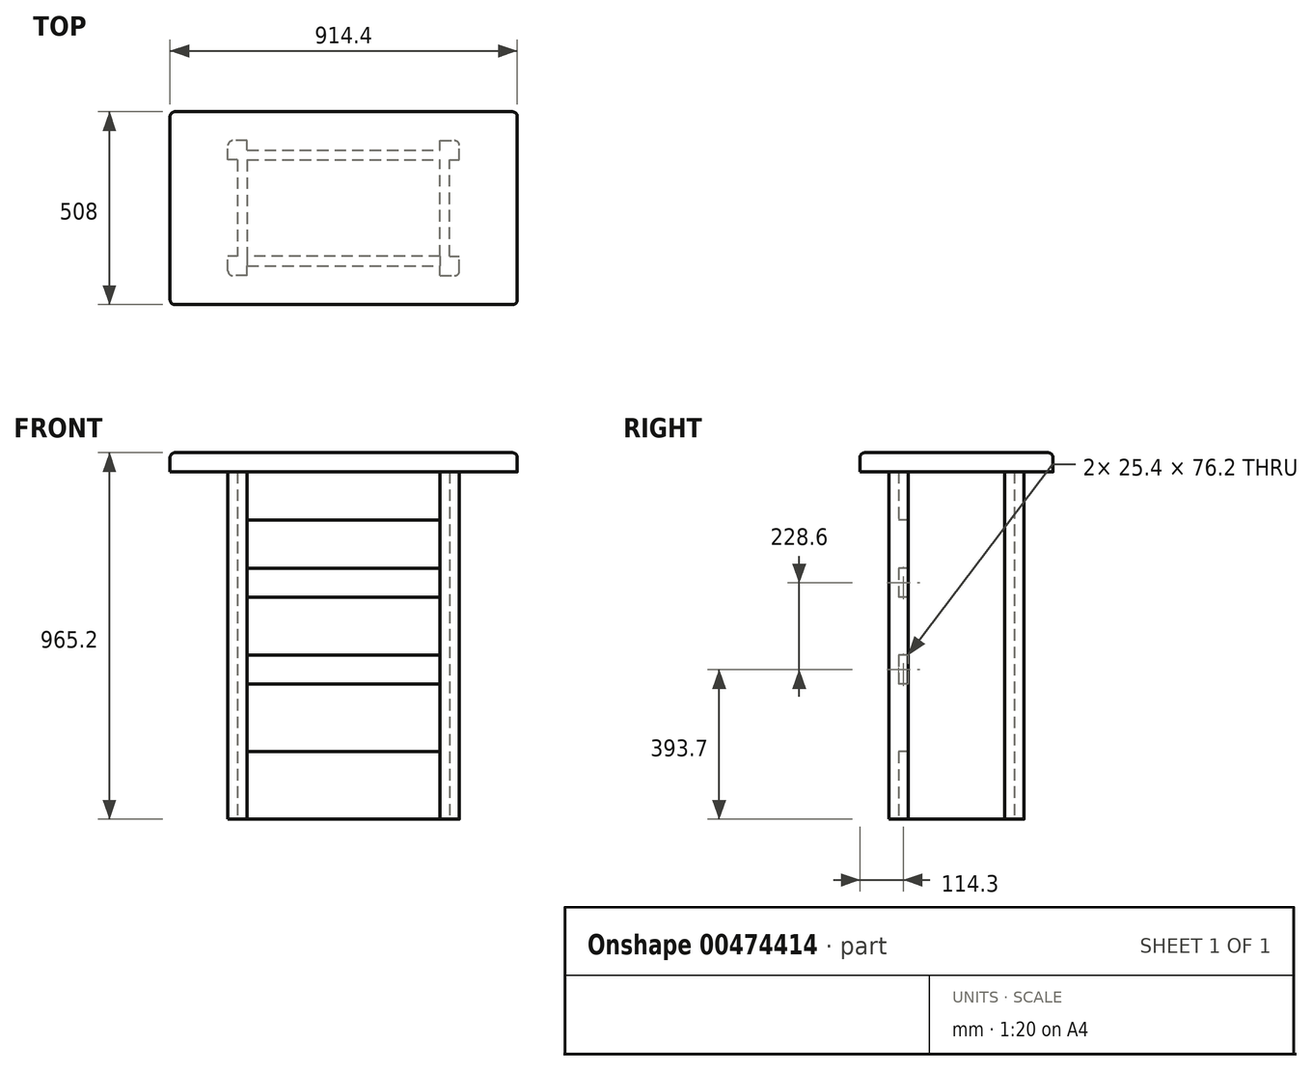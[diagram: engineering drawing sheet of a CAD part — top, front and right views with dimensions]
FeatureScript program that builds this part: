
annotation { "Feature Type Name" : "Feature", "Feature Type Description" : "" }
export const myFeature = defineFeature(function(context is Context, id is Id, definition is map)
    precondition{}
    {
        {
            var Q0;
            Q0=qCreatedBy(makeId("Top.planeOp"),FACE);
            var sketch = newSketch(context, id + "F0", { "sketchPlane" : qUnion([Q0])});
            skLineSegment(sketch, "E0.bottom", {"start": v(254, -177.8) * mm, "end": v(304.8, -177.8) * mm});
            skLineSegment(sketch, "E0.top", {"start": v(254, -127) * mm, "end": v(304.8, -127) * mm});
            skLineSegment(sketch, "E0.left", {"start": v(254, -177.8) * mm, "end": v(254, -127) * mm});
            skLineSegment(sketch, "E0.right", {"start": v(304.8, -177.8) * mm, "end": v(304.8, -127) * mm});
            skLineSegment(sketch, "E1.bottom", {"start": v(254, 127) * mm, "end": v(304.8, 127) * mm});
            skLineSegment(sketch, "E1.top", {"start": v(254, 177.8) * mm, "end": v(304.8, 177.8) * mm});
            skLineSegment(sketch, "E1.left", {"start": v(254, 127) * mm, "end": v(254, 177.8) * mm});
            skLineSegment(sketch, "E1.right", {"start": v(304.8, 127) * mm, "end": v(304.8, 177.8) * mm});
            skLineSegment(sketch, "E2.MirrorCS", {"start": v(-304.8, -177.8) * mm, "end": v(-304.8, -127) * mm});
            skLineSegment(sketch, "E3.MirrorCS", {"start": v(-254, -177.8) * mm, "end": v(-254, -127) * mm});
            skLineSegment(sketch, "E4.MirrorCS", {"start": v(-254, 177.8) * mm, "end": v(-304.8, 177.8) * mm});
            skLineSegment(sketch, "E5.MirrorCS", {"start": v(-254, -177.8) * mm, "end": v(-304.8, -177.8) * mm});
            skLineSegment(sketch, "E6.MirrorCS", {"start": v(-304.8, 127) * mm, "end": v(-304.8, 177.8) * mm});
            skLineSegment(sketch, "E7.MirrorCS", {"start": v(-254, 127) * mm, "end": v(-254, 177.8) * mm});
            skLineSegment(sketch, "E8.MirrorCS", {"start": v(-254, -127) * mm, "end": v(-304.8, -127) * mm});
            skLineSegment(sketch, "E9.MirrorCS", {"start": v(-254, 127) * mm, "end": v(-304.8, 127) * mm});
            skLineSegment(sketch, "E10.bottom", {"start": v(-254, 127) * mm, "end": v(254, 127) * mm});
            skLineSegment(sketch, "E10.top", {"start": v(-254, 152.4) * mm, "end": v(254, 152.4) * mm});
            skLineSegment(sketch, "E10.left", {"start": v(-254, 127) * mm, "end": v(-254, 152.4) * mm});
            skLineSegment(sketch, "E10.right", {"start": v(254, 127) * mm, "end": v(254, 152.4) * mm});
            skLineSegment(sketch, "E11.bottom", {"start": v(-254, 127) * mm, "end": v(-279.4, 127) * mm});
            skLineSegment(sketch, "E11.top", {"start": v(-254, -127) * mm, "end": v(-279.4, -127) * mm});
            skLineSegment(sketch, "E11.left", {"start": v(-254, 127) * mm, "end": v(-254, -127) * mm});
            skLineSegment(sketch, "E11.right", {"start": v(-279.4, 127) * mm, "end": v(-279.4, -127) * mm});
            skLineSegment(sketch, "E12.bottom", {"start": v(-254, -127) * mm, "end": v(254, -127) * mm});
            skLineSegment(sketch, "E12.top", {"start": v(-254, -152.4) * mm, "end": v(254, -152.4) * mm});
            skLineSegment(sketch, "E12.left", {"start": v(-254, -127) * mm, "end": v(-254, -152.4) * mm});
            skLineSegment(sketch, "E12.right", {"start": v(254, -127) * mm, "end": v(254, -152.4) * mm});
            skLineSegment(sketch, "E13.bottom", {"start": v(254, -127) * mm, "end": v(279.4, -127) * mm});
            skLineSegment(sketch, "E13.top", {"start": v(254, 127) * mm, "end": v(279.4, 127) * mm});
            skLineSegment(sketch, "E13.left", {"start": v(254, -127) * mm, "end": v(254, 127) * mm});
            skLineSegment(sketch, "E13.right", {"start": v(279.4, -127) * mm, "end": v(279.4, 127) * mm});
            skSolve(sketch);
        }
        {
            var Q0;
            {var subQ4=sQuery(id+"F0.wireOp",EDGE,"E4.MirrorCS");Q0=makeQuery(id+"F0.imprint","IMPRINT",FACE,{"disambiguationData":[TD([[makeQuery(id+"F0.imprint","IMPRINT",EDGE,{"derivedFrom":subQ4}),1.0]])]});}
            var Q1;
            {var subQ5=sQuery(id+"F0.wireOp",EDGE,"E2.MirrorCS");Q1=makeQuery(id+"F0.imprint","IMPRINT",FACE,{"disambiguationData":[TD([[makeQuery(id+"F0.imprint","IMPRINT",EDGE,{"derivedFrom":subQ5}),-1.0]])]});}
            var Q2;
            {var subQ6=sQuery(id+"F0.wireOp",EDGE,"E0.bottom");Q2=makeQuery(id+"F0.imprint","IMPRINT",FACE,{"disambiguationData":[TD([[makeQuery(id+"F0.imprint","IMPRINT",EDGE,{"derivedFrom":subQ6}),1.0]])]});}
            var Q3;
            {var subQ1=sQuery(id+"F0.wireOp",EDGE,"E1.top");Q3=makeQuery(id+"F0.imprint","IMPRINT",FACE,{"disambiguationData":[TD([[makeQuery(id+"F0.imprint","IMPRINT",EDGE,{"derivedFrom":subQ1}),-1.0]])]});}
            var Q4;
            {var subQ0=sQuery(id+"F0.wireOp",EDGE,"E11.left");Q4=makeQuery(id+"F0.imprint","IMPRINT",FACE,{"disambiguationData":[TD([[makeQuery(id+"F0.imprint","IMPRINT",EDGE,{"derivedFrom":subQ0}),-1.0]])]});}
            var Q5;
            {var subQ2=sQuery(id+"F0.wireOp",EDGE,"E10.bottom");Q5=makeQuery(id+"F0.imprint","IMPRINT",FACE,{"disambiguationData":[TD([[makeQuery(id+"F0.imprint","IMPRINT",EDGE,{"derivedFrom":subQ2}),1.0]])]});}
            var Q6;
            {var subQ2=sQuery(id+"F0.wireOp",EDGE,"E13.left");Q6=makeQuery(id+"F0.imprint","IMPRINT",FACE,{"disambiguationData":[TD([[makeQuery(id+"F0.imprint","IMPRINT",EDGE,{"derivedFrom":subQ2}),-1.0]])]});}
            var Q7;
            {var subQ2=sQuery(id+"F0.wireOp",EDGE,"E12.bottom");Q7=makeQuery(id+"F0.imprint","IMPRINT",FACE,{"disambiguationData":[TD([[makeQuery(id+"F0.imprint","IMPRINT",EDGE,{"derivedFrom":subQ2}),-1.0]])]});}
            extrude(context, id + "F1", {"entities" : qUnion([Q0, Q1, Q2, Q3, Q4, Q5, Q6, Q7]), "depth" : 914.4 * mm, "offsetDistance" : 25.4 * mm});
        }
        {
            var Q0;
            Q0=makeQuery(id+"F1.opExtrude","CAP_FACE",FACE,{"disambiguationData":[OSD([sQuery(id+"F0.wireOp",EDGE,"E0.bottom"),sQuery(id+"F0.wireOp",EDGE,"E0.top"),sQuery(id+"F0.wireOp",EDGE,"E0.left"),sQuery(id+"F0.wireOp",EDGE,"E0.right"),sQuery(id+"F0.wireOp",EDGE,"E1.bottom"),sQuery(id+"F0.wireOp",EDGE,"E1.top"),sQuery(id+"F0.wireOp",EDGE,"E1.left"),sQuery(id+"F0.wireOp",EDGE,"E1.right"),sQuery(id+"F0.wireOp",EDGE,"E2.MirrorCS"),sQuery(id+"F0.wireOp",EDGE,"E3.MirrorCS"),sQuery(id+"F0.wireOp",EDGE,"E4.MirrorCS"),sQuery(id+"F0.wireOp",EDGE,"E5.MirrorCS"),sQuery(id+"F0.wireOp",EDGE,"E6.MirrorCS"),sQuery(id+"F0.wireOp",EDGE,"E7.MirrorCS"),sQuery(id+"F0.wireOp",EDGE,"E8.MirrorCS"),sQuery(id+"F0.wireOp",EDGE,"E9.MirrorCS"),sQuery(id+"F0.wireOp",EDGE,"E10.bottom"),sQuery(id+"F0.wireOp",EDGE,"E10.top"),sQuery(id+"F0.wireOp",EDGE,"E11.left"),sQuery(id+"F0.wireOp",EDGE,"E11.right"),sQuery(id+"F0.wireOp",EDGE,"E12.bottom"),sQuery(id+"F0.wireOp",EDGE,"E12.top"),sQuery(id+"F0.wireOp",EDGE,"E13.left"),sQuery(id+"F0.wireOp",EDGE,"E13.right")])],"isStart":false});
            var sketch = newSketch(context, id + "F2", { "sketchPlane" : qUnion([Q0])});
            skLineSegment(sketch, "E14.bottom", {"start": v(-457.2, 254) * mm, "end": v(457.2, 254) * mm});
            skLineSegment(sketch, "E14.top", {"start": v(-457.2, -254) * mm, "end": v(457.2, -254) * mm});
            skLineSegment(sketch, "E14.left", {"start": v(-457.2, 254) * mm, "end": v(-457.2, -254) * mm});
            skLineSegment(sketch, "E14.right", {"start": v(457.2, 254) * mm, "end": v(457.2, -254) * mm});
            skSolve(sketch);
        }
        {
            var Q0;
            Q0 = qSketchRegion(id + "F2", true);
            extrude(context, id + "F3", {"entities" : qUnion([Q0]), "operationType" : NewBodyOperationType.ADD, "depth" : 50.8 * mm, "offsetDistance" : 25.4 * mm});
        }
        {
            var Q0;
            Q0=makeQuery(id+"F1.opExtrude","SWEPT_FACE",FACE,{"disambiguationData":[OSD([sQuery(id+"F0.wireOp",EDGE,"E12.top")])]});
            var sketch = newSketch(context, id + "F4", { "sketchPlane" : qUnion([Q0])});
            skLineSegment(sketch, "E15.bottom", {"start": v(-254, 787.4) * mm, "end": v(254, 787.4) * mm});
            skLineSegment(sketch, "E15.top", {"start": v(-254, 660.4) * mm, "end": v(254, 660.4) * mm});
            skLineSegment(sketch, "E15.left", {"start": v(-254, 787.4) * mm, "end": v(-254, 660.4) * mm});
            skLineSegment(sketch, "E15.right", {"start": v(254, 787.4) * mm, "end": v(254, 660.4) * mm});
            skLineSegment(sketch, "E16.bottom", {"start": v(-254, 584.2) * mm, "end": v(254, 584.2) * mm});
            skLineSegment(sketch, "E16.top", {"start": v(-254, 431.8) * mm, "end": v(254, 431.8) * mm});
            skLineSegment(sketch, "E16.left", {"start": v(-254, 584.2) * mm, "end": v(-254, 431.8) * mm});
            skLineSegment(sketch, "E16.right", {"start": v(254, 584.2) * mm, "end": v(254, 431.8) * mm});
            skLineSegment(sketch, "E17.bottom", {"start": v(-254, 355.6) * mm, "end": v(254, 355.6) * mm});
            skLineSegment(sketch, "E17.top", {"start": v(-254, 177.8) * mm, "end": v(254, 177.8) * mm});
            skLineSegment(sketch, "E17.left", {"start": v(-254, 355.6) * mm, "end": v(-254, 177.8) * mm});
            skLineSegment(sketch, "E17.right", {"start": v(254, 355.6) * mm, "end": v(254, 177.8) * mm});
            skSolve(sketch);
        }
        {
            var Q0;
            Q0=makeQuery(id+"F4.imprint","IMPRINT",FACE,{"disambiguationData":[TD([[makeQuery(id+"F4.imprint","IMPRINT",EDGE,{"derivedFrom":sQuery(id+"F4.wireOp",EDGE,"E15.bottom")}),-1.0]])]});
            var Q1;
            Q1=makeQuery(id+"F4.imprint","IMPRINT",FACE,{"disambiguationData":[TD([[makeQuery(id+"F4.imprint","IMPRINT",EDGE,{"derivedFrom":sQuery(id+"F4.wireOp",EDGE,"E16.bottom")}),-1.0]])]});
            var Q2;
            Q2=makeQuery(id+"F4.imprint","IMPRINT",FACE,{"disambiguationData":[TD([[makeQuery(id+"F4.imprint","IMPRINT",EDGE,{"derivedFrom":sQuery(id+"F4.wireOp",EDGE,"E17.bottom")}),-1.0]])]});
            extrude(context, id + "F5", {"entities" : qUnion([Q0, Q1, Q2]), "operationType" : NewBodyOperationType.REMOVE, "oppositeDirection" : true, "depth" : 127 * mm, "offsetDistance" : 25.4 * mm});
        }
        {
            var Q0;
            Q0=makeQuery(id+"F3.opExtrude","CAP_EDGE",EDGE,{"disambiguationData":[OSD([sQuery(id+"F2.wireOp",EDGE,"E14.right")])],"isStart":false});
            var Q1;
            Q1=makeQuery(id+"F3.opExtrude","CAP_EDGE",EDGE,{"disambiguationData":[OSD([sQuery(id+"F2.wireOp",EDGE,"E14.top")])],"isStart":false});
            var Q2;
            Q2=makeQuery(id+"F3.opExtrude","CAP_EDGE",EDGE,{"disambiguationData":[OSD([sQuery(id+"F2.wireOp",EDGE,"E14.left")])],"isStart":false});
            var Q3;
            Q3=makeQuery(id+"F3.opExtrude","CAP_EDGE",EDGE,{"disambiguationData":[OSD([sQuery(id+"F2.wireOp",EDGE,"E14.bottom")])],"isStart":false});
            var Q4;
            Q4=makeQuery(id+"F3.opExtrude","SWEPT_EDGE",EDGE,{"disambiguationData":[OSD([sQuery(id+"F2.wireOp",EDGE,"E14.top"),sQuery(id+"F2.wireOp",EDGE,"E14.right")])]});
            var Q5;
            Q5=makeQuery(id+"F3.opExtrude","SWEPT_EDGE",EDGE,{"disambiguationData":[OSD([sQuery(id+"F2.wireOp",EDGE,"E14.top"),sQuery(id+"F2.wireOp",EDGE,"E14.left")])]});
            var Q6;
            Q6=makeQuery(id+"F3.opExtrude","SWEPT_EDGE",EDGE,{"disambiguationData":[OSD([sQuery(id+"F2.wireOp",EDGE,"E14.bottom"),sQuery(id+"F2.wireOp",EDGE,"E14.right")])]});
            var Q7;
            Q7=makeQuery(id+"F3.opExtrude","SWEPT_EDGE",EDGE,{"disambiguationData":[OSD([sQuery(id+"F2.wireOp",EDGE,"E14.bottom"),sQuery(id+"F2.wireOp",EDGE,"E14.left")])]});
            var Q8;
            Q8=makeQuery(id+"F1.opExtrude","SWEPT_EDGE",EDGE,{"disambiguationData":[OSD([sQuery(id+"F0.wireOp",EDGE,"E0.bottom"),sQuery(id+"F0.wireOp",EDGE,"E0.right")])]});
            var Q9;
            Q9=makeQuery(id+"F1.opExtrude","SWEPT_EDGE",EDGE,{"disambiguationData":[OSD([sQuery(id+"F0.wireOp",EDGE,"E2.MirrorCS"),sQuery(id+"F0.wireOp",EDGE,"E5.MirrorCS")])]});
            var Q10;
            Q10=makeQuery(id+"F1.opExtrude","SWEPT_EDGE",EDGE,{"disambiguationData":[OSD([sQuery(id+"F0.wireOp",EDGE,"E1.top"),sQuery(id+"F0.wireOp",EDGE,"E1.right")])]});
            var Q11;
            Q11=makeQuery(id+"F1.opExtrude","SWEPT_EDGE",EDGE,{"disambiguationData":[OSD([sQuery(id+"F0.wireOp",EDGE,"E4.MirrorCS"),sQuery(id+"F0.wireOp",EDGE,"E6.MirrorCS")])]});
            fillet(context, id + "F6", {"entities" : qUnion([Q0, Q1, Q2, Q3, Q4, Q5, Q6, Q7, Q8, Q9, Q10, Q11]), "radius" : 12.7 * mm, "tangentPropagation" : true, "allowEdgeOverflow" : false});
        }
    });
